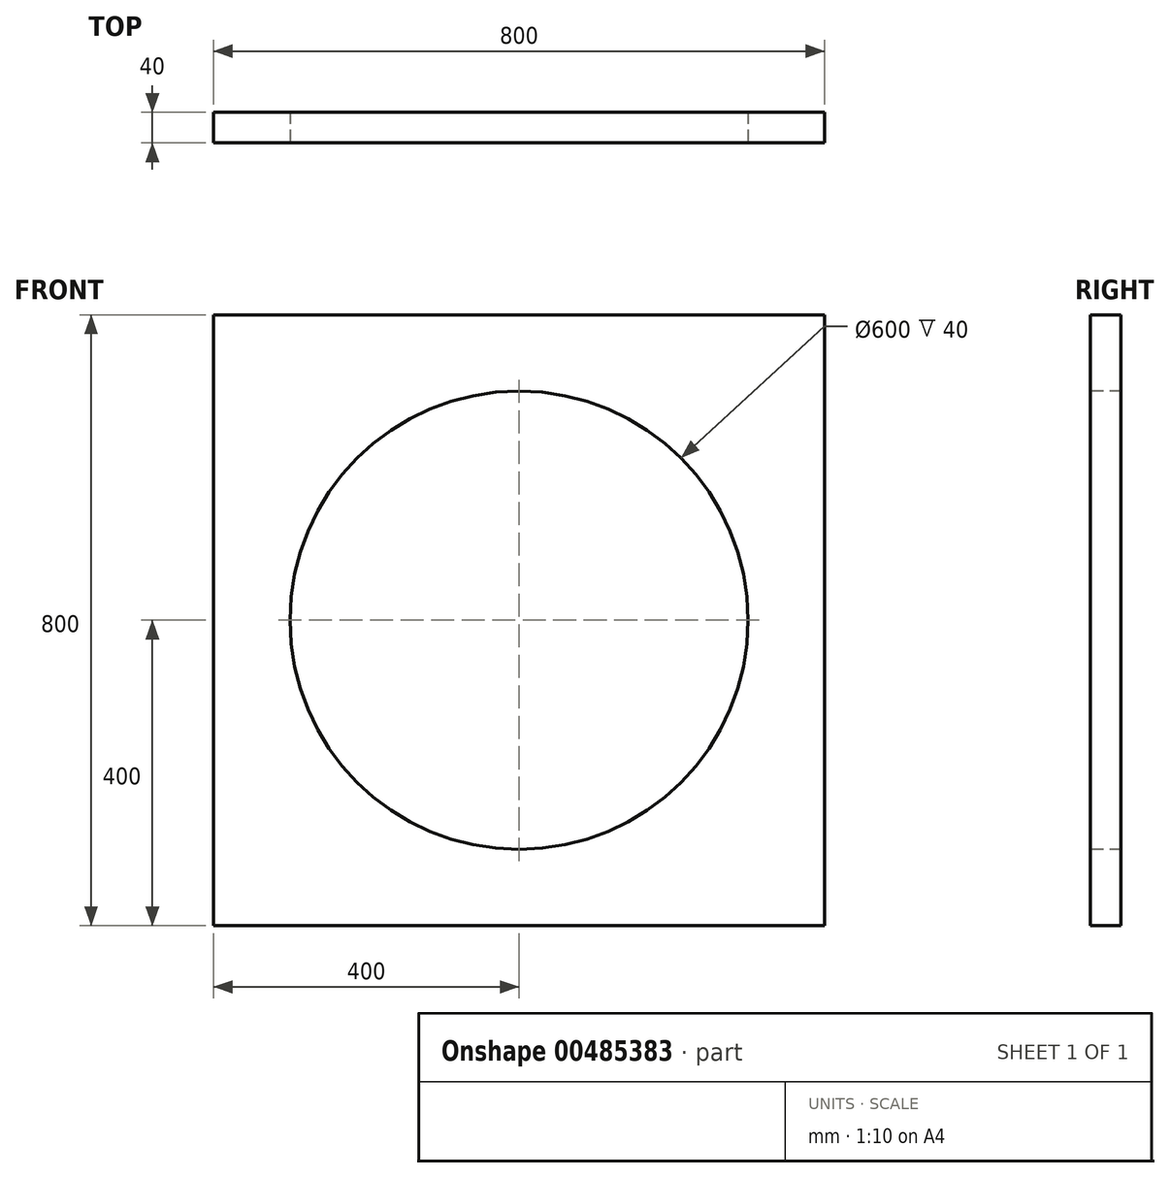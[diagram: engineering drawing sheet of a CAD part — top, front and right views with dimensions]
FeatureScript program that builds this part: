
annotation { "Feature Type Name" : "Feature", "Feature Type Description" : "" }
export const myFeature = defineFeature(function(context is Context, id is Id, definition is map)
    precondition{}
    {
        {
            var Q0;
            Q0=qCreatedBy(makeId("Front.planeOp"),FACE);
            var sketch = newSketch(context, id + "F0", { "sketchPlane" : qUnion([Q0])});
            skLineSegment(sketch, "E0.bottom", {"start": v(-400, 400) * mm, "end": v(400, 400) * mm});
            skLineSegment(sketch, "E0.top", {"start": v(-400, -400) * mm, "end": v(400, -400) * mm});
            skLineSegment(sketch, "E0.left", {"start": v(-400, 400) * mm, "end": v(-400, -400) * mm});
            skLineSegment(sketch, "E0.right", {"start": v(400, 400) * mm, "end": v(400, -400) * mm});
            skPoint(sketch, "E0.middle", {"position": v(0, 0) * mm});
            skSolve(sketch);
        }
        {
            var Q0;
            Q0 = qSketchRegion(id + "F0", true);
            extrude(context, id + "F1", {"entities" : qUnion([Q0]), "oppositeDirection" : true, "depth" : 40 * mm});
        }
        {
            var Q0;
            Q0=makeQuery(id+"F1.opExtrude","CAP_FACE",FACE,{"disambiguationData":[OSD([sQuery(id+"F0.wireOp",EDGE,"E0.bottom"),sQuery(id+"F0.wireOp",EDGE,"E0.top"),sQuery(id+"F0.wireOp",EDGE,"E0.left"),sQuery(id+"F0.wireOp",EDGE,"E0.right")])],"isStart":true});
            var sketch = newSketch(context, id + "F2", { "sketchPlane" : qUnion([Q0])});
            skCircle(sketch, "E1", {"center": v(0, 0) * mm, "radius": 300 * mm});
            skSolve(sketch);
        }
        {
            var Q0;
            Q0 = qSketchRegion(id + "F2", true);
            extrude(context, id + "F3", {"entities" : qUnion([Q0]), "operationType" : NewBodyOperationType.REMOVE, "oppositeDirection" : true, "depth" : 40 * mm});
        }
    });
